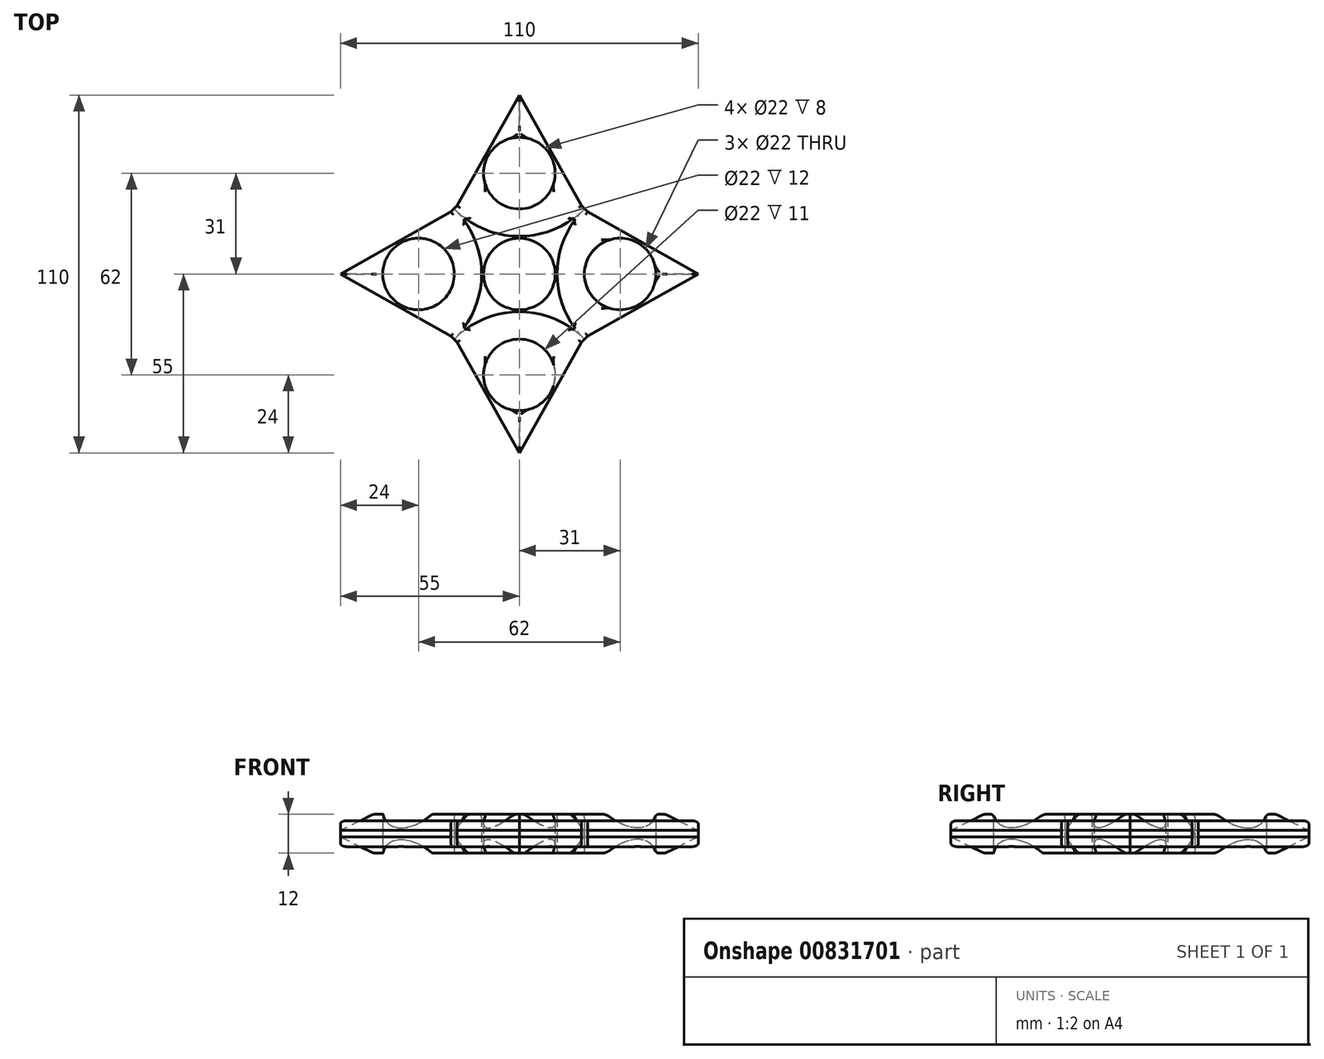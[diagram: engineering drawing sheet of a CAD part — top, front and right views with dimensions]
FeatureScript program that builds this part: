
annotation { "Feature Type Name" : "Feature", "Feature Type Description" : "" }
export const myFeature = defineFeature(function(context is Context, id is Id, definition is map)
    precondition{}
    {
        {
            var Q0;
            Q0=qCreatedBy(makeId("Top.planeOp"),FACE);
            var sketch = newSketch(context, id + "F0", { "sketchPlane" : qUnion([Q0])});
            skLineSegment(sketch, "E0.bottom", {"start": v(-55, 55) * mm, "end": v(55, 55) * mm});
            skLineSegment(sketch, "E0.top", {"start": v(-55, -55) * mm, "end": v(55, -55) * mm});
            skLineSegment(sketch, "E0.left", {"start": v(-55, 55) * mm, "end": v(-55, -55) * mm});
            skLineSegment(sketch, "E0.right", {"start": v(55, 55) * mm, "end": v(55, -55) * mm});
            skPoint(sketch, "E0.middle", {"position": v(0, 0) * mm});
            skCircle(sketch, "E1", {"center": v(0, 0) * mm, "radius": 11 * mm});
            skCircle(sketch, "E2", {"center": v(-31, 0) * mm, "radius": 11 * mm});
            skCircle(sketch, "E3.MirrorC", {"center": v(31, 0) * mm, "radius": 11 * mm});
            skCircle(sketch, "E4", {"center": v(0, 31) * mm, "radius": 11 * mm});
            skCircle(sketch, "E5.MirrorC", {"center": v(0, -31) * mm, "radius": 11 * mm});
            skLineSegment(sketch, "E6", {"start": v(0, 0) * mm, "end": v(-19.8, 19.8) * mm, "construction": true});
            skLineSegment(sketch, "E7.MirrorCS", {"start": v(0, 0) * mm, "end": v(19.8, 19.8) * mm, "construction": true});
            skLineSegment(sketch, "E8.MirrorCS", {"start": v(0, 0) * mm, "end": v(19.8, -19.8) * mm, "construction": true});
            skLineSegment(sketch, "E9.MirrorCS", {"start": v(0, 0) * mm, "end": v(-19.8, -19.8) * mm, "construction": true});
            skLineSegment(sketch, "E10", {"start": v(-55, 0) * mm, "end": v(-19.8, 19.8) * mm});
            skLineSegment(sketch, "E11", {"start": v(-19.8, 19.8) * mm, "end": v(0, 55) * mm});
            skLineSegment(sketch, "E12.MirrorCS", {"start": v(19.8, 19.8) * mm, "end": v(0, 55) * mm});
            skLineSegment(sketch, "E13.MirrorCS", {"start": v(55, 0) * mm, "end": v(19.8, 19.8) * mm});
            skLineSegment(sketch, "E14.MirrorCS", {"start": v(55, 0) * mm, "end": v(19.8, -19.8) * mm});
            skLineSegment(sketch, "E15.MirrorCS", {"start": v(19.8, -19.8) * mm, "end": v(0, -55) * mm});
            skLineSegment(sketch, "E16.MirrorCS", {"start": v(-19.8, -19.8) * mm, "end": v(0, -55) * mm});
            skLineSegment(sketch, "E17.MirrorCS", {"start": v(-55, 0) * mm, "end": v(-19.8, -19.8) * mm});
            skSolve(sketch);
        }
        {
            var Q0;
            Q0=makeQuery(id+"F0.imprint","IMPRINT",FACE,{"disambiguationData":[TD([[makeQuery(id+"F0.imprint","IMPRINT",EDGE,{"derivedFrom":sQuery(id+"F0.wireOp",EDGE,"E1")}),-1.0]])]});
            extrude(context, id + "F1", {"entities" : qUnion([Q0]), "depth" : 8 * mm, "offsetDistance" : 25 * mm});
        }
        {
            var Q0;
            Q0=makeQuery(id+"F1.opExtrude","CAP_FACE",FACE,{"disambiguationData":[OSD([sQuery(id+"F0.wireOp",EDGE,"E1"),sQuery(id+"F0.wireOp",EDGE,"E3.MirrorC"),sQuery(id+"F0.wireOp",EDGE,"E2"),sQuery(id+"F0.wireOp",EDGE,"E4"),sQuery(id+"F0.wireOp",EDGE,"E5.MirrorC"),sQuery(id+"F0.wireOp",EDGE,"E10"),sQuery(id+"F0.wireOp",EDGE,"E11"),sQuery(id+"F0.wireOp",EDGE,"E12.MirrorCS"),sQuery(id+"F0.wireOp",EDGE,"E13.MirrorCS"),sQuery(id+"F0.wireOp",EDGE,"E14.MirrorCS"),sQuery(id+"F0.wireOp",EDGE,"E15.MirrorCS"),sQuery(id+"F0.wireOp",EDGE,"E16.MirrorCS"),sQuery(id+"F0.wireOp",EDGE,"E17.MirrorCS")])],"isStart":false});
            var sketch = newSketch(context, id + "F2", { "sketchPlane" : qUnion([Q0])});
            skLineSegment(sketch, "E18", {"start": v(0, 0) * mm, "end": v(-19.8, 19.8) * mm, "construction": true});
            skLineSegment(sketch, "E19.MirrorCS", {"start": v(0, 0) * mm, "end": v(19.8, 19.8) * mm, "construction": true});
            skLineSegment(sketch, "E20.MirrorCS", {"start": v(0, 0) * mm, "end": v(-19.8, -19.8) * mm, "construction": true});
            skLineSegment(sketch, "E21.MirrorCS", {"start": v(0, 0) * mm, "end": v(19.8, -19.8) * mm, "construction": true});
            skArc(sketch, "E22", {"start": v(-19.8, -19.8) * mm, "mid": v(-11.6, 0) * mm, "end": v(-19.8, 19.8) * mm});
            skArc(sketch, "E23", {"start": v(-19.8, 19.8) * mm, "mid": v(0, 11.6) * mm, "end": v(19.8, 19.8) * mm});
            skArc(sketch, "E24", {"start": v(19.8, 19.8) * mm, "mid": v(11.6, 0) * mm, "end": v(19.8, -19.8) * mm});
            skArc(sketch, "E25", {"start": v(19.8, -19.8) * mm, "mid": v(0, -11.6) * mm, "end": v(-19.8, -19.8) * mm});
            skSolve(sketch);
        }
        {
            var Q0;
            Q0=makeQuery(id+"F2.imprint","IMPRINT",FACE,{"disambiguationData":[TD([[makeQuery(id+"F2.imprint","IMPRINT",EDGE,{"derivedFrom":sQuery(id+"F2.wireOp",EDGE,"E25")}),1.0]])]});
            var Q1;
            Q1=makeQuery(id+"F2.imprint","IMPRINT",FACE,{"disambiguationData":[TD([[makeQuery(id+"F2.imprint","IMPRINT",EDGE,{"derivedFrom":sQuery(id+"F2.wireOp",EDGE,"E22")}),1.0]])]});
            var Q2;
            Q2=makeQuery(id+"F2.imprint","IMPRINT",FACE,{"disambiguationData":[TD([[makeQuery(id+"F2.imprint","IMPRINT",EDGE,{"derivedFrom":sQuery(id+"F2.wireOp",EDGE,"E23")}),1.0]])]});
            var Q3;
            Q3=makeQuery(id+"F2.imprint","IMPRINT",FACE,{"disambiguationData":[TD([[makeQuery(id+"F2.imprint","IMPRINT",EDGE,{"derivedFrom":sQuery(id+"F2.wireOp",EDGE,"E24")}),1.0]])]});
            extrude(context, id + "F3", {"entities" : qUnion([Q0, Q1, Q2, Q3]), "depth" : 2 * mm, "offsetDistance" : 25 * mm, "hasSecondDirection" : true, "secondDirectionOppositeDirection" : true, "secondDirectionDepth" : 10 * mm});
        }
        {
            var Q0;
            Q0=makeQuery(id+"F3.opExtrude","CAP_EDGE",EDGE,{"disambiguationData":[OSD([sQuery(id+"F0.wireOp",EDGE,"E15.MirrorCS")])],"isStart":true});
            var Q1;
            Q1=makeQuery(id+"F3.opExtrude","CAP_EDGE",EDGE,{"disambiguationData":[OSD([sQuery(id+"F0.wireOp",EDGE,"E16.MirrorCS")])],"isStart":true});
            var Q2;
            Q2=makeQuery(id+"F3.opExtrude","CAP_EDGE",EDGE,{"disambiguationData":[OSD([sQuery(id+"F0.wireOp",EDGE,"E14.MirrorCS")])],"isStart":true});
            var Q3;
            Q3=makeQuery(id+"F3.opExtrude","CAP_EDGE",EDGE,{"disambiguationData":[OSD([sQuery(id+"F0.wireOp",EDGE,"E13.MirrorCS")])],"isStart":true});
            var Q4;
            Q4=makeQuery(id+"F3.opExtrude","CAP_EDGE",EDGE,{"disambiguationData":[OSD([sQuery(id+"F0.wireOp",EDGE,"E12.MirrorCS")])],"isStart":true});
            var Q5;
            Q5=makeQuery(id+"F3.opExtrude","CAP_EDGE",EDGE,{"disambiguationData":[OSD([sQuery(id+"F0.wireOp",EDGE,"E11")])],"isStart":true});
            var Q6;
            Q6=makeQuery(id+"F3.opExtrude","CAP_EDGE",EDGE,{"disambiguationData":[OSD([sQuery(id+"F0.wireOp",EDGE,"E10")])],"isStart":true});
            var Q7;
            Q7=makeQuery(id+"F3.opExtrude","CAP_EDGE",EDGE,{"disambiguationData":[OSD([sQuery(id+"F0.wireOp",EDGE,"E17.MirrorCS")])],"isStart":true});
            var Q8;
            Q8=makeQuery(id+"F3.opExtrude","CAP_EDGE",EDGE,{"disambiguationData":[OSD([sQuery(id+"F0.wireOp",EDGE,"E17.MirrorCS")])],"isStart":false});
            var Q9;
            Q9=makeQuery(id+"F3.opExtrude","CAP_EDGE",EDGE,{"disambiguationData":[OSD([sQuery(id+"F0.wireOp",EDGE,"E10")])],"isStart":false});
            var Q10;
            Q10=makeQuery(id+"F3.opExtrude","CAP_EDGE",EDGE,{"disambiguationData":[OSD([sQuery(id+"F0.wireOp",EDGE,"E11")])],"isStart":false});
            var Q11;
            Q11=makeQuery(id+"F3.opExtrude","CAP_EDGE",EDGE,{"disambiguationData":[OSD([sQuery(id+"F0.wireOp",EDGE,"E12.MirrorCS")])],"isStart":false});
            var Q12;
            Q12=makeQuery(id+"F3.opExtrude","CAP_EDGE",EDGE,{"disambiguationData":[OSD([sQuery(id+"F0.wireOp",EDGE,"E13.MirrorCS")])],"isStart":false});
            var Q13;
            Q13=makeQuery(id+"F3.opExtrude","CAP_EDGE",EDGE,{"disambiguationData":[OSD([sQuery(id+"F0.wireOp",EDGE,"E14.MirrorCS")])],"isStart":false});
            var Q14;
            Q14=makeQuery(id+"F3.opExtrude","CAP_EDGE",EDGE,{"disambiguationData":[OSD([sQuery(id+"F0.wireOp",EDGE,"E15.MirrorCS")])],"isStart":false});
            var Q15;
            Q15=makeQuery(id+"F3.opExtrude","CAP_EDGE",EDGE,{"disambiguationData":[OSD([sQuery(id+"F0.wireOp",EDGE,"E16.MirrorCS")])],"isStart":false});
            chamfer(context, id + "F4", {"entities" : qUnion([Q0, Q1, Q2, Q3, Q4, Q5, Q6, Q7, Q8, Q9, Q10, Q11, Q12, Q13, Q14, Q15]), "width" : 5 * mm, "tangentPropagation" : true});
        }
        {
            var Q0;
            Q0=makeQuery(id+"F1.opExtrude","SWEPT_EDGE",EDGE,{"disambiguationData":[OSD([sQuery(id+"F0.wireOp",EDGE,"E16.MirrorCS"),sQuery(id+"F0.wireOp",EDGE,"E17.MirrorCS")])]});
            var Q1;
            Q1=makeQuery(id+"F1.opExtrude","SWEPT_EDGE",EDGE,{"disambiguationData":[OSD([sQuery(id+"F0.wireOp",EDGE,"E10"),sQuery(id+"F0.wireOp",EDGE,"E11")])]});
            var Q2;
            Q2=makeQuery(id+"F1.opExtrude","SWEPT_EDGE",EDGE,{"disambiguationData":[OSD([sQuery(id+"F0.wireOp",EDGE,"E12.MirrorCS"),sQuery(id+"F0.wireOp",EDGE,"E13.MirrorCS")])]});
            var Q3;
            Q3=makeQuery(id+"F1.opExtrude","SWEPT_EDGE",EDGE,{"disambiguationData":[OSD([sQuery(id+"F0.wireOp",EDGE,"E14.MirrorCS"),sQuery(id+"F0.wireOp",EDGE,"E15.MirrorCS")])]});
            chamfer(context, id + "F5", {"entities" : qUnion([Q0, Q1, Q2, Q3]), "width" : 5 * mm, "tangentPropagation" : true});
        }
        {
            var Q0;
            Q0=makeQuery(id+"F1.opExtrude","CAP_EDGE",EDGE,{"disambiguationData":[OSD([sQuery(id+"F0.wireOp",EDGE,"E12.MirrorCS")])],"isStart":false});
            var Q1;
            {var subQ0=sQuery(id+"F0.wireOp",EDGE,"E13.MirrorCS");var subQ1=sQuery(id+"F0.wireOp",EDGE,"E12.MirrorCS");Q1=makeQuery(id+"F5.opChamfer","BLEND_EDGE",EDGE,{"blendedFrom":[makeQuery(id+"F1.opExtrude","SWEPT_EDGE",EDGE,{"disambiguationData":[OSD([subQ1,subQ0])]}),makeQuery(id+"F1.opExtrude","CAP_FACE",FACE,{"disambiguationData":[OSD([sQuery(id+"F0.wireOp",EDGE,"E1"),sQuery(id+"F0.wireOp",EDGE,"E3.MirrorC"),sQuery(id+"F0.wireOp",EDGE,"E2"),sQuery(id+"F0.wireOp",EDGE,"E4"),sQuery(id+"F0.wireOp",EDGE,"E5.MirrorC"),sQuery(id+"F0.wireOp",EDGE,"E10"),sQuery(id+"F0.wireOp",EDGE,"E11"),subQ1,subQ0,sQuery(id+"F0.wireOp",EDGE,"E14.MirrorCS"),sQuery(id+"F0.wireOp",EDGE,"E15.MirrorCS"),sQuery(id+"F0.wireOp",EDGE,"E16.MirrorCS"),sQuery(id+"F0.wireOp",EDGE,"E17.MirrorCS")])],"isStart":false})],"blendedInto":[makeQuery(id+"F1.opExtrude","CAP_FACE",FACE,{"disambiguationData":[OSD([sQuery(id+"F0.wireOp",EDGE,"E1"),sQuery(id+"F0.wireOp",EDGE,"E3.MirrorC"),sQuery(id+"F0.wireOp",EDGE,"E2"),sQuery(id+"F0.wireOp",EDGE,"E4"),sQuery(id+"F0.wireOp",EDGE,"E5.MirrorC"),sQuery(id+"F0.wireOp",EDGE,"E10"),sQuery(id+"F0.wireOp",EDGE,"E11"),subQ1,subQ0,sQuery(id+"F0.wireOp",EDGE,"E14.MirrorCS"),sQuery(id+"F0.wireOp",EDGE,"E15.MirrorCS"),sQuery(id+"F0.wireOp",EDGE,"E16.MirrorCS"),sQuery(id+"F0.wireOp",EDGE,"E17.MirrorCS")])],"isStart":false})]});}
            var Q2;
            Q2=makeQuery(id+"F1.opExtrude","CAP_EDGE",EDGE,{"disambiguationData":[OSD([sQuery(id+"F0.wireOp",EDGE,"E13.MirrorCS")])],"isStart":false});
            var Q3;
            Q3=makeQuery(id+"F1.opExtrude","CAP_EDGE",EDGE,{"disambiguationData":[OSD([sQuery(id+"F0.wireOp",EDGE,"E14.MirrorCS")])],"isStart":false});
            var Q4;
            {var subQ0=sQuery(id+"F0.wireOp",EDGE,"E15.MirrorCS");var subQ1=sQuery(id+"F0.wireOp",EDGE,"E14.MirrorCS");Q4=makeQuery(id+"F5.opChamfer","BLEND_EDGE",EDGE,{"blendedFrom":[makeQuery(id+"F1.opExtrude","SWEPT_EDGE",EDGE,{"disambiguationData":[OSD([subQ1,subQ0])]}),makeQuery(id+"F1.opExtrude","CAP_FACE",FACE,{"disambiguationData":[OSD([sQuery(id+"F0.wireOp",EDGE,"E1"),sQuery(id+"F0.wireOp",EDGE,"E3.MirrorC"),sQuery(id+"F0.wireOp",EDGE,"E2"),sQuery(id+"F0.wireOp",EDGE,"E4"),sQuery(id+"F0.wireOp",EDGE,"E5.MirrorC"),sQuery(id+"F0.wireOp",EDGE,"E10"),sQuery(id+"F0.wireOp",EDGE,"E11"),sQuery(id+"F0.wireOp",EDGE,"E12.MirrorCS"),sQuery(id+"F0.wireOp",EDGE,"E13.MirrorCS"),subQ1,subQ0,sQuery(id+"F0.wireOp",EDGE,"E16.MirrorCS"),sQuery(id+"F0.wireOp",EDGE,"E17.MirrorCS")])],"isStart":false})],"blendedInto":[makeQuery(id+"F1.opExtrude","CAP_FACE",FACE,{"disambiguationData":[OSD([sQuery(id+"F0.wireOp",EDGE,"E1"),sQuery(id+"F0.wireOp",EDGE,"E3.MirrorC"),sQuery(id+"F0.wireOp",EDGE,"E2"),sQuery(id+"F0.wireOp",EDGE,"E4"),sQuery(id+"F0.wireOp",EDGE,"E5.MirrorC"),sQuery(id+"F0.wireOp",EDGE,"E10"),sQuery(id+"F0.wireOp",EDGE,"E11"),sQuery(id+"F0.wireOp",EDGE,"E12.MirrorCS"),sQuery(id+"F0.wireOp",EDGE,"E13.MirrorCS"),subQ1,subQ0,sQuery(id+"F0.wireOp",EDGE,"E16.MirrorCS"),sQuery(id+"F0.wireOp",EDGE,"E17.MirrorCS")])],"isStart":false})]});}
            var Q5;
            Q5=makeQuery(id+"F1.opExtrude","CAP_EDGE",EDGE,{"disambiguationData":[OSD([sQuery(id+"F0.wireOp",EDGE,"E15.MirrorCS")])],"isStart":false});
            var Q6;
            Q6=makeQuery(id+"F1.opExtrude","CAP_EDGE",EDGE,{"disambiguationData":[OSD([sQuery(id+"F0.wireOp",EDGE,"E16.MirrorCS")])],"isStart":false});
            var Q7;
            {var subQ0=sQuery(id+"F0.wireOp",EDGE,"E17.MirrorCS");var subQ1=sQuery(id+"F0.wireOp",EDGE,"E16.MirrorCS");Q7=makeQuery(id+"F5.opChamfer","BLEND_EDGE",EDGE,{"blendedFrom":[makeQuery(id+"F1.opExtrude","SWEPT_EDGE",EDGE,{"disambiguationData":[OSD([subQ1,subQ0])]}),makeQuery(id+"F1.opExtrude","CAP_FACE",FACE,{"disambiguationData":[OSD([sQuery(id+"F0.wireOp",EDGE,"E1"),sQuery(id+"F0.wireOp",EDGE,"E3.MirrorC"),sQuery(id+"F0.wireOp",EDGE,"E2"),sQuery(id+"F0.wireOp",EDGE,"E4"),sQuery(id+"F0.wireOp",EDGE,"E5.MirrorC"),sQuery(id+"F0.wireOp",EDGE,"E10"),sQuery(id+"F0.wireOp",EDGE,"E11"),sQuery(id+"F0.wireOp",EDGE,"E12.MirrorCS"),sQuery(id+"F0.wireOp",EDGE,"E13.MirrorCS"),sQuery(id+"F0.wireOp",EDGE,"E14.MirrorCS"),sQuery(id+"F0.wireOp",EDGE,"E15.MirrorCS"),subQ1,subQ0])],"isStart":false})],"blendedInto":[makeQuery(id+"F1.opExtrude","CAP_FACE",FACE,{"disambiguationData":[OSD([sQuery(id+"F0.wireOp",EDGE,"E1"),sQuery(id+"F0.wireOp",EDGE,"E3.MirrorC"),sQuery(id+"F0.wireOp",EDGE,"E2"),sQuery(id+"F0.wireOp",EDGE,"E4"),sQuery(id+"F0.wireOp",EDGE,"E5.MirrorC"),sQuery(id+"F0.wireOp",EDGE,"E10"),sQuery(id+"F0.wireOp",EDGE,"E11"),sQuery(id+"F0.wireOp",EDGE,"E12.MirrorCS"),sQuery(id+"F0.wireOp",EDGE,"E13.MirrorCS"),sQuery(id+"F0.wireOp",EDGE,"E14.MirrorCS"),sQuery(id+"F0.wireOp",EDGE,"E15.MirrorCS"),subQ1,subQ0])],"isStart":false})]});}
            var Q8;
            Q8=makeQuery(id+"F1.opExtrude","CAP_EDGE",EDGE,{"disambiguationData":[OSD([sQuery(id+"F0.wireOp",EDGE,"E17.MirrorCS")])],"isStart":false});
            var Q9;
            Q9=makeQuery(id+"F1.opExtrude","CAP_EDGE",EDGE,{"disambiguationData":[OSD([sQuery(id+"F0.wireOp",EDGE,"E10")])],"isStart":false});
            var Q10;
            {var subQ0=sQuery(id+"F0.wireOp",EDGE,"E11");var subQ1=sQuery(id+"F0.wireOp",EDGE,"E10");Q10=makeQuery(id+"F5.opChamfer","BLEND_EDGE",EDGE,{"blendedFrom":[makeQuery(id+"F1.opExtrude","SWEPT_EDGE",EDGE,{"disambiguationData":[OSD([subQ1,subQ0])]}),makeQuery(id+"F1.opExtrude","CAP_FACE",FACE,{"disambiguationData":[OSD([sQuery(id+"F0.wireOp",EDGE,"E1"),sQuery(id+"F0.wireOp",EDGE,"E3.MirrorC"),sQuery(id+"F0.wireOp",EDGE,"E2"),sQuery(id+"F0.wireOp",EDGE,"E4"),sQuery(id+"F0.wireOp",EDGE,"E5.MirrorC"),subQ1,subQ0,sQuery(id+"F0.wireOp",EDGE,"E12.MirrorCS"),sQuery(id+"F0.wireOp",EDGE,"E13.MirrorCS"),sQuery(id+"F0.wireOp",EDGE,"E14.MirrorCS"),sQuery(id+"F0.wireOp",EDGE,"E15.MirrorCS"),sQuery(id+"F0.wireOp",EDGE,"E16.MirrorCS"),sQuery(id+"F0.wireOp",EDGE,"E17.MirrorCS")])],"isStart":false})],"blendedInto":[makeQuery(id+"F1.opExtrude","CAP_FACE",FACE,{"disambiguationData":[OSD([sQuery(id+"F0.wireOp",EDGE,"E1"),sQuery(id+"F0.wireOp",EDGE,"E3.MirrorC"),sQuery(id+"F0.wireOp",EDGE,"E2"),sQuery(id+"F0.wireOp",EDGE,"E4"),sQuery(id+"F0.wireOp",EDGE,"E5.MirrorC"),subQ1,subQ0,sQuery(id+"F0.wireOp",EDGE,"E12.MirrorCS"),sQuery(id+"F0.wireOp",EDGE,"E13.MirrorCS"),sQuery(id+"F0.wireOp",EDGE,"E14.MirrorCS"),sQuery(id+"F0.wireOp",EDGE,"E15.MirrorCS"),sQuery(id+"F0.wireOp",EDGE,"E16.MirrorCS"),sQuery(id+"F0.wireOp",EDGE,"E17.MirrorCS")])],"isStart":false})]});}
            var Q11;
            Q11=makeQuery(id+"F1.opExtrude","CAP_EDGE",EDGE,{"disambiguationData":[OSD([sQuery(id+"F0.wireOp",EDGE,"E11")])],"isStart":false});
            var Q12;
            {var subQ0=sQuery(id+"F0.wireOp",EDGE,"E17.MirrorCS");var subQ1=sQuery(id+"F0.wireOp",EDGE,"E16.MirrorCS");Q12=makeQuery(id+"F5.opChamfer","BLEND_EDGE",EDGE,{"blendedFrom":[makeQuery(id+"F1.opExtrude","SWEPT_EDGE",EDGE,{"disambiguationData":[OSD([subQ1,subQ0])]}),makeQuery(id+"F1.opExtrude","CAP_FACE",FACE,{"disambiguationData":[OSD([sQuery(id+"F0.wireOp",EDGE,"E1"),sQuery(id+"F0.wireOp",EDGE,"E3.MirrorC"),sQuery(id+"F0.wireOp",EDGE,"E2"),sQuery(id+"F0.wireOp",EDGE,"E4"),sQuery(id+"F0.wireOp",EDGE,"E5.MirrorC"),sQuery(id+"F0.wireOp",EDGE,"E10"),sQuery(id+"F0.wireOp",EDGE,"E11"),sQuery(id+"F0.wireOp",EDGE,"E12.MirrorCS"),sQuery(id+"F0.wireOp",EDGE,"E13.MirrorCS"),sQuery(id+"F0.wireOp",EDGE,"E14.MirrorCS"),sQuery(id+"F0.wireOp",EDGE,"E15.MirrorCS"),subQ1,subQ0])],"isStart":true})],"blendedInto":[makeQuery(id+"F1.opExtrude","CAP_FACE",FACE,{"disambiguationData":[OSD([sQuery(id+"F0.wireOp",EDGE,"E1"),sQuery(id+"F0.wireOp",EDGE,"E3.MirrorC"),sQuery(id+"F0.wireOp",EDGE,"E2"),sQuery(id+"F0.wireOp",EDGE,"E4"),sQuery(id+"F0.wireOp",EDGE,"E5.MirrorC"),sQuery(id+"F0.wireOp",EDGE,"E10"),sQuery(id+"F0.wireOp",EDGE,"E11"),sQuery(id+"F0.wireOp",EDGE,"E12.MirrorCS"),sQuery(id+"F0.wireOp",EDGE,"E13.MirrorCS"),sQuery(id+"F0.wireOp",EDGE,"E14.MirrorCS"),sQuery(id+"F0.wireOp",EDGE,"E15.MirrorCS"),subQ1,subQ0])],"isStart":true})]});}
            var Q13;
            Q13=makeQuery(id+"F1.opExtrude","CAP_EDGE",EDGE,{"disambiguationData":[OSD([sQuery(id+"F0.wireOp",EDGE,"E17.MirrorCS")])],"isStart":true});
            var Q14;
            Q14=makeQuery(id+"F1.opExtrude","CAP_EDGE",EDGE,{"disambiguationData":[OSD([sQuery(id+"F0.wireOp",EDGE,"E16.MirrorCS")])],"isStart":true});
            var Q15;
            Q15=makeQuery(id+"F1.opExtrude","CAP_EDGE",EDGE,{"disambiguationData":[OSD([sQuery(id+"F0.wireOp",EDGE,"E15.MirrorCS")])],"isStart":true});
            var Q16;
            {var subQ0=sQuery(id+"F0.wireOp",EDGE,"E15.MirrorCS");var subQ1=sQuery(id+"F0.wireOp",EDGE,"E14.MirrorCS");Q16=makeQuery(id+"F5.opChamfer","BLEND_EDGE",EDGE,{"blendedFrom":[makeQuery(id+"F1.opExtrude","SWEPT_EDGE",EDGE,{"disambiguationData":[OSD([subQ1,subQ0])]}),makeQuery(id+"F1.opExtrude","CAP_FACE",FACE,{"disambiguationData":[OSD([sQuery(id+"F0.wireOp",EDGE,"E1"),sQuery(id+"F0.wireOp",EDGE,"E3.MirrorC"),sQuery(id+"F0.wireOp",EDGE,"E2"),sQuery(id+"F0.wireOp",EDGE,"E4"),sQuery(id+"F0.wireOp",EDGE,"E5.MirrorC"),sQuery(id+"F0.wireOp",EDGE,"E10"),sQuery(id+"F0.wireOp",EDGE,"E11"),sQuery(id+"F0.wireOp",EDGE,"E12.MirrorCS"),sQuery(id+"F0.wireOp",EDGE,"E13.MirrorCS"),subQ1,subQ0,sQuery(id+"F0.wireOp",EDGE,"E16.MirrorCS"),sQuery(id+"F0.wireOp",EDGE,"E17.MirrorCS")])],"isStart":true})],"blendedInto":[makeQuery(id+"F1.opExtrude","CAP_FACE",FACE,{"disambiguationData":[OSD([sQuery(id+"F0.wireOp",EDGE,"E1"),sQuery(id+"F0.wireOp",EDGE,"E3.MirrorC"),sQuery(id+"F0.wireOp",EDGE,"E2"),sQuery(id+"F0.wireOp",EDGE,"E4"),sQuery(id+"F0.wireOp",EDGE,"E5.MirrorC"),sQuery(id+"F0.wireOp",EDGE,"E10"),sQuery(id+"F0.wireOp",EDGE,"E11"),sQuery(id+"F0.wireOp",EDGE,"E12.MirrorCS"),sQuery(id+"F0.wireOp",EDGE,"E13.MirrorCS"),subQ1,subQ0,sQuery(id+"F0.wireOp",EDGE,"E16.MirrorCS"),sQuery(id+"F0.wireOp",EDGE,"E17.MirrorCS")])],"isStart":true})]});}
            var Q17;
            Q17=makeQuery(id+"F1.opExtrude","CAP_EDGE",EDGE,{"disambiguationData":[OSD([sQuery(id+"F0.wireOp",EDGE,"E14.MirrorCS")])],"isStart":true});
            var Q18;
            Q18=makeQuery(id+"F1.opExtrude","CAP_EDGE",EDGE,{"disambiguationData":[OSD([sQuery(id+"F0.wireOp",EDGE,"E10")])],"isStart":true});
            var Q19;
            {var subQ0=sQuery(id+"F0.wireOp",EDGE,"E11");var subQ1=sQuery(id+"F0.wireOp",EDGE,"E10");Q19=makeQuery(id+"F5.opChamfer","BLEND_EDGE",EDGE,{"blendedFrom":[makeQuery(id+"F1.opExtrude","SWEPT_EDGE",EDGE,{"disambiguationData":[OSD([subQ1,subQ0])]}),makeQuery(id+"F1.opExtrude","CAP_FACE",FACE,{"disambiguationData":[OSD([sQuery(id+"F0.wireOp",EDGE,"E1"),sQuery(id+"F0.wireOp",EDGE,"E3.MirrorC"),sQuery(id+"F0.wireOp",EDGE,"E2"),sQuery(id+"F0.wireOp",EDGE,"E4"),sQuery(id+"F0.wireOp",EDGE,"E5.MirrorC"),subQ1,subQ0,sQuery(id+"F0.wireOp",EDGE,"E12.MirrorCS"),sQuery(id+"F0.wireOp",EDGE,"E13.MirrorCS"),sQuery(id+"F0.wireOp",EDGE,"E14.MirrorCS"),sQuery(id+"F0.wireOp",EDGE,"E15.MirrorCS"),sQuery(id+"F0.wireOp",EDGE,"E16.MirrorCS"),sQuery(id+"F0.wireOp",EDGE,"E17.MirrorCS")])],"isStart":true})],"blendedInto":[makeQuery(id+"F1.opExtrude","CAP_FACE",FACE,{"disambiguationData":[OSD([sQuery(id+"F0.wireOp",EDGE,"E1"),sQuery(id+"F0.wireOp",EDGE,"E3.MirrorC"),sQuery(id+"F0.wireOp",EDGE,"E2"),sQuery(id+"F0.wireOp",EDGE,"E4"),sQuery(id+"F0.wireOp",EDGE,"E5.MirrorC"),subQ1,subQ0,sQuery(id+"F0.wireOp",EDGE,"E12.MirrorCS"),sQuery(id+"F0.wireOp",EDGE,"E13.MirrorCS"),sQuery(id+"F0.wireOp",EDGE,"E14.MirrorCS"),sQuery(id+"F0.wireOp",EDGE,"E15.MirrorCS"),sQuery(id+"F0.wireOp",EDGE,"E16.MirrorCS"),sQuery(id+"F0.wireOp",EDGE,"E17.MirrorCS")])],"isStart":true})]});}
            var Q20;
            Q20=makeQuery(id+"F1.opExtrude","CAP_EDGE",EDGE,{"disambiguationData":[OSD([sQuery(id+"F0.wireOp",EDGE,"E11")])],"isStart":true});
            var Q21;
            Q21=makeQuery(id+"F1.opExtrude","CAP_EDGE",EDGE,{"disambiguationData":[OSD([sQuery(id+"F0.wireOp",EDGE,"E12.MirrorCS")])],"isStart":true});
            var Q22;
            {var subQ0=sQuery(id+"F0.wireOp",EDGE,"E13.MirrorCS");var subQ1=sQuery(id+"F0.wireOp",EDGE,"E12.MirrorCS");Q22=makeQuery(id+"F5.opChamfer","BLEND_EDGE",EDGE,{"blendedFrom":[makeQuery(id+"F1.opExtrude","SWEPT_EDGE",EDGE,{"disambiguationData":[OSD([subQ1,subQ0])]}),makeQuery(id+"F1.opExtrude","CAP_FACE",FACE,{"disambiguationData":[OSD([sQuery(id+"F0.wireOp",EDGE,"E1"),sQuery(id+"F0.wireOp",EDGE,"E3.MirrorC"),sQuery(id+"F0.wireOp",EDGE,"E2"),sQuery(id+"F0.wireOp",EDGE,"E4"),sQuery(id+"F0.wireOp",EDGE,"E5.MirrorC"),sQuery(id+"F0.wireOp",EDGE,"E10"),sQuery(id+"F0.wireOp",EDGE,"E11"),subQ1,subQ0,sQuery(id+"F0.wireOp",EDGE,"E14.MirrorCS"),sQuery(id+"F0.wireOp",EDGE,"E15.MirrorCS"),sQuery(id+"F0.wireOp",EDGE,"E16.MirrorCS"),sQuery(id+"F0.wireOp",EDGE,"E17.MirrorCS")])],"isStart":true})],"blendedInto":[makeQuery(id+"F1.opExtrude","CAP_FACE",FACE,{"disambiguationData":[OSD([sQuery(id+"F0.wireOp",EDGE,"E1"),sQuery(id+"F0.wireOp",EDGE,"E3.MirrorC"),sQuery(id+"F0.wireOp",EDGE,"E2"),sQuery(id+"F0.wireOp",EDGE,"E4"),sQuery(id+"F0.wireOp",EDGE,"E5.MirrorC"),sQuery(id+"F0.wireOp",EDGE,"E10"),sQuery(id+"F0.wireOp",EDGE,"E11"),subQ1,subQ0,sQuery(id+"F0.wireOp",EDGE,"E14.MirrorCS"),sQuery(id+"F0.wireOp",EDGE,"E15.MirrorCS"),sQuery(id+"F0.wireOp",EDGE,"E16.MirrorCS"),sQuery(id+"F0.wireOp",EDGE,"E17.MirrorCS")])],"isStart":true})]});}
            var Q23;
            Q23=makeQuery(id+"F1.opExtrude","CAP_EDGE",EDGE,{"disambiguationData":[OSD([sQuery(id+"F0.wireOp",EDGE,"E13.MirrorCS")])],"isStart":true});
            var Q24;
            {var subQ0=sQuery(id+"F0.wireOp",EDGE,"E12.MirrorCS");Q24=makeQuery(id+"F4.opChamfer","BLEND_EDGE",EDGE,{"blendedFrom":[makeQuery(id+"F3.opExtrude","CAP_EDGE",EDGE,{"disambiguationData":[OSD([subQ0])],"isStart":true}),makeQuery(id+"F3.opExtrude","CAP_FACE",FACE,{"disambiguationData":[OSD([sQuery(id+"F0.wireOp",EDGE,"E4"),sQuery(id+"F0.wireOp",EDGE,"E11"),subQ0,sQuery(id+"F2.wireOp",EDGE,"E23")])],"isStart":true})],"blendedInto":[makeQuery(id+"F3.opExtrude","CAP_FACE",FACE,{"disambiguationData":[OSD([sQuery(id+"F0.wireOp",EDGE,"E4"),sQuery(id+"F0.wireOp",EDGE,"E11"),subQ0,sQuery(id+"F2.wireOp",EDGE,"E23")])],"isStart":true})]});}
            var Q25;
            {var subQ0=sQuery(id+"F0.wireOp",EDGE,"E13.MirrorCS");Q25=makeQuery(id+"F4.opChamfer","BLEND_EDGE",EDGE,{"blendedFrom":[makeQuery(id+"F3.opExtrude","CAP_EDGE",EDGE,{"disambiguationData":[OSD([subQ0])],"isStart":true}),makeQuery(id+"F3.opExtrude","CAP_FACE",FACE,{"disambiguationData":[OSD([sQuery(id+"F0.wireOp",EDGE,"E3.MirrorC"),subQ0,sQuery(id+"F0.wireOp",EDGE,"E14.MirrorCS"),sQuery(id+"F2.wireOp",EDGE,"E24")])],"isStart":true})],"blendedInto":[makeQuery(id+"F3.opExtrude","CAP_FACE",FACE,{"disambiguationData":[OSD([sQuery(id+"F0.wireOp",EDGE,"E3.MirrorC"),subQ0,sQuery(id+"F0.wireOp",EDGE,"E14.MirrorCS"),sQuery(id+"F2.wireOp",EDGE,"E24")])],"isStart":true})]});}
            var Q26;
            {var subQ0=sQuery(id+"F0.wireOp",EDGE,"E11");Q26=makeQuery(id+"F4.opChamfer","BLEND_EDGE",EDGE,{"blendedFrom":[makeQuery(id+"F3.opExtrude","CAP_EDGE",EDGE,{"disambiguationData":[OSD([subQ0])],"isStart":true}),makeQuery(id+"F3.opExtrude","CAP_FACE",FACE,{"disambiguationData":[OSD([sQuery(id+"F0.wireOp",EDGE,"E4"),subQ0,sQuery(id+"F0.wireOp",EDGE,"E12.MirrorCS"),sQuery(id+"F2.wireOp",EDGE,"E23")])],"isStart":true})],"blendedInto":[makeQuery(id+"F3.opExtrude","CAP_FACE",FACE,{"disambiguationData":[OSD([sQuery(id+"F0.wireOp",EDGE,"E4"),subQ0,sQuery(id+"F0.wireOp",EDGE,"E12.MirrorCS"),sQuery(id+"F2.wireOp",EDGE,"E23")])],"isStart":true})]});}
            var Q27;
            {var subQ0=sQuery(id+"F0.wireOp",EDGE,"E10");Q27=makeQuery(id+"F4.opChamfer","BLEND_EDGE",EDGE,{"blendedFrom":[makeQuery(id+"F3.opExtrude","CAP_EDGE",EDGE,{"disambiguationData":[OSD([subQ0])],"isStart":true}),makeQuery(id+"F3.opExtrude","CAP_FACE",FACE,{"disambiguationData":[OSD([sQuery(id+"F0.wireOp",EDGE,"E2"),subQ0,sQuery(id+"F0.wireOp",EDGE,"E17.MirrorCS"),sQuery(id+"F2.wireOp",EDGE,"E22")])],"isStart":true})],"blendedInto":[makeQuery(id+"F3.opExtrude","CAP_FACE",FACE,{"disambiguationData":[OSD([sQuery(id+"F0.wireOp",EDGE,"E2"),subQ0,sQuery(id+"F0.wireOp",EDGE,"E17.MirrorCS"),sQuery(id+"F2.wireOp",EDGE,"E22")])],"isStart":true})]});}
            var Q28;
            {var subQ0=sQuery(id+"F0.wireOp",EDGE,"E17.MirrorCS");Q28=makeQuery(id+"F4.opChamfer","BLEND_EDGE",EDGE,{"blendedFrom":[makeQuery(id+"F3.opExtrude","CAP_EDGE",EDGE,{"disambiguationData":[OSD([subQ0])],"isStart":true}),makeQuery(id+"F3.opExtrude","CAP_FACE",FACE,{"disambiguationData":[OSD([sQuery(id+"F0.wireOp",EDGE,"E2"),sQuery(id+"F0.wireOp",EDGE,"E10"),subQ0,sQuery(id+"F2.wireOp",EDGE,"E22")])],"isStart":true})],"blendedInto":[makeQuery(id+"F3.opExtrude","CAP_FACE",FACE,{"disambiguationData":[OSD([sQuery(id+"F0.wireOp",EDGE,"E2"),sQuery(id+"F0.wireOp",EDGE,"E10"),subQ0,sQuery(id+"F2.wireOp",EDGE,"E22")])],"isStart":true})]});}
            var Q29;
            {var subQ0=sQuery(id+"F0.wireOp",EDGE,"E16.MirrorCS");Q29=makeQuery(id+"F4.opChamfer","BLEND_EDGE",EDGE,{"blendedFrom":[makeQuery(id+"F3.opExtrude","CAP_EDGE",EDGE,{"disambiguationData":[OSD([subQ0])],"isStart":true}),makeQuery(id+"F3.opExtrude","CAP_FACE",FACE,{"disambiguationData":[OSD([sQuery(id+"F0.wireOp",EDGE,"E5.MirrorC"),sQuery(id+"F0.wireOp",EDGE,"E15.MirrorCS"),subQ0,sQuery(id+"F2.wireOp",EDGE,"E25")])],"isStart":true})],"blendedInto":[makeQuery(id+"F3.opExtrude","CAP_FACE",FACE,{"disambiguationData":[OSD([sQuery(id+"F0.wireOp",EDGE,"E5.MirrorC"),sQuery(id+"F0.wireOp",EDGE,"E15.MirrorCS"),subQ0,sQuery(id+"F2.wireOp",EDGE,"E25")])],"isStart":true})]});}
            var Q30;
            {var subQ0=sQuery(id+"F0.wireOp",EDGE,"E15.MirrorCS");Q30=makeQuery(id+"F4.opChamfer","BLEND_EDGE",EDGE,{"blendedFrom":[makeQuery(id+"F3.opExtrude","CAP_EDGE",EDGE,{"disambiguationData":[OSD([subQ0])],"isStart":true}),makeQuery(id+"F3.opExtrude","CAP_FACE",FACE,{"disambiguationData":[OSD([sQuery(id+"F0.wireOp",EDGE,"E5.MirrorC"),subQ0,sQuery(id+"F0.wireOp",EDGE,"E16.MirrorCS"),sQuery(id+"F2.wireOp",EDGE,"E25")])],"isStart":true})],"blendedInto":[makeQuery(id+"F3.opExtrude","CAP_FACE",FACE,{"disambiguationData":[OSD([sQuery(id+"F0.wireOp",EDGE,"E5.MirrorC"),subQ0,sQuery(id+"F0.wireOp",EDGE,"E16.MirrorCS"),sQuery(id+"F2.wireOp",EDGE,"E25")])],"isStart":true})]});}
            var Q31;
            {var subQ0=sQuery(id+"F0.wireOp",EDGE,"E14.MirrorCS");Q31=makeQuery(id+"F4.opChamfer","BLEND_EDGE",EDGE,{"blendedFrom":[makeQuery(id+"F3.opExtrude","CAP_EDGE",EDGE,{"disambiguationData":[OSD([subQ0])],"isStart":true}),makeQuery(id+"F3.opExtrude","CAP_FACE",FACE,{"disambiguationData":[OSD([sQuery(id+"F0.wireOp",EDGE,"E3.MirrorC"),sQuery(id+"F0.wireOp",EDGE,"E13.MirrorCS"),subQ0,sQuery(id+"F2.wireOp",EDGE,"E24")])],"isStart":true})],"blendedInto":[makeQuery(id+"F3.opExtrude","CAP_FACE",FACE,{"disambiguationData":[OSD([sQuery(id+"F0.wireOp",EDGE,"E3.MirrorC"),sQuery(id+"F0.wireOp",EDGE,"E13.MirrorCS"),subQ0,sQuery(id+"F2.wireOp",EDGE,"E24")])],"isStart":true})]});}
            var Q32;
            Q32=makeQuery(id+"F3.opExtrude","CAP_EDGE",EDGE,{"disambiguationData":[OSD([sQuery(id+"F2.wireOp",EDGE,"E25")])],"isStart":true});
            var Q33;
            Q33=makeQuery(id+"F3.opExtrude","CAP_EDGE",EDGE,{"disambiguationData":[OSD([sQuery(id+"F2.wireOp",EDGE,"E24")])],"isStart":true});
            var Q34;
            Q34=makeQuery(id+"F3.opExtrude","CAP_EDGE",EDGE,{"disambiguationData":[OSD([sQuery(id+"F2.wireOp",EDGE,"E22")])],"isStart":true});
            var Q35;
            Q35=makeQuery(id+"F3.opExtrude","CAP_EDGE",EDGE,{"disambiguationData":[OSD([sQuery(id+"F2.wireOp",EDGE,"E23")])],"isStart":true});
            var Q36;
            Q36=makeQuery(id+"F1.opExtrude","CAP_EDGE",EDGE,{"disambiguationData":[OSD([sQuery(id+"F0.wireOp",EDGE,"E1")])],"isStart":true});
            var Q37;
            {var subQ0=sQuery(id+"F0.wireOp",EDGE,"E10");Q37=makeQuery(id+"F4.opChamfer","BLEND_EDGE",EDGE,{"blendedFrom":[makeQuery(id+"F3.opExtrude","CAP_EDGE",EDGE,{"disambiguationData":[OSD([subQ0])],"isStart":false}),makeQuery(id+"F3.opExtrude","CAP_FACE",FACE,{"disambiguationData":[OSD([sQuery(id+"F0.wireOp",EDGE,"E2"),subQ0,sQuery(id+"F0.wireOp",EDGE,"E17.MirrorCS"),sQuery(id+"F2.wireOp",EDGE,"E22")])],"isStart":false})],"blendedInto":[makeQuery(id+"F3.opExtrude","CAP_FACE",FACE,{"disambiguationData":[OSD([sQuery(id+"F0.wireOp",EDGE,"E2"),subQ0,sQuery(id+"F0.wireOp",EDGE,"E17.MirrorCS"),sQuery(id+"F2.wireOp",EDGE,"E22")])],"isStart":false})]});}
            var Q38;
            {var subQ0=sQuery(id+"F0.wireOp",EDGE,"E17.MirrorCS");Q38=makeQuery(id+"F4.opChamfer","BLEND_EDGE",EDGE,{"blendedFrom":[makeQuery(id+"F3.opExtrude","CAP_EDGE",EDGE,{"disambiguationData":[OSD([subQ0])],"isStart":false}),makeQuery(id+"F3.opExtrude","CAP_FACE",FACE,{"disambiguationData":[OSD([sQuery(id+"F0.wireOp",EDGE,"E2"),sQuery(id+"F0.wireOp",EDGE,"E10"),subQ0,sQuery(id+"F2.wireOp",EDGE,"E22")])],"isStart":false})],"blendedInto":[makeQuery(id+"F3.opExtrude","CAP_FACE",FACE,{"disambiguationData":[OSD([sQuery(id+"F0.wireOp",EDGE,"E2"),sQuery(id+"F0.wireOp",EDGE,"E10"),subQ0,sQuery(id+"F2.wireOp",EDGE,"E22")])],"isStart":false})]});}
            var Q39;
            {var subQ0=sQuery(id+"F0.wireOp",EDGE,"E16.MirrorCS");Q39=makeQuery(id+"F4.opChamfer","BLEND_EDGE",EDGE,{"blendedFrom":[makeQuery(id+"F3.opExtrude","CAP_EDGE",EDGE,{"disambiguationData":[OSD([subQ0])],"isStart":false}),makeQuery(id+"F3.opExtrude","CAP_FACE",FACE,{"disambiguationData":[OSD([sQuery(id+"F0.wireOp",EDGE,"E5.MirrorC"),sQuery(id+"F0.wireOp",EDGE,"E15.MirrorCS"),subQ0,sQuery(id+"F2.wireOp",EDGE,"E25")])],"isStart":false})],"blendedInto":[makeQuery(id+"F3.opExtrude","CAP_FACE",FACE,{"disambiguationData":[OSD([sQuery(id+"F0.wireOp",EDGE,"E5.MirrorC"),sQuery(id+"F0.wireOp",EDGE,"E15.MirrorCS"),subQ0,sQuery(id+"F2.wireOp",EDGE,"E25")])],"isStart":false})]});}
            var Q40;
            {var subQ0=sQuery(id+"F0.wireOp",EDGE,"E15.MirrorCS");Q40=makeQuery(id+"F4.opChamfer","BLEND_EDGE",EDGE,{"blendedFrom":[makeQuery(id+"F3.opExtrude","CAP_EDGE",EDGE,{"disambiguationData":[OSD([subQ0])],"isStart":false}),makeQuery(id+"F3.opExtrude","CAP_FACE",FACE,{"disambiguationData":[OSD([sQuery(id+"F0.wireOp",EDGE,"E5.MirrorC"),subQ0,sQuery(id+"F0.wireOp",EDGE,"E16.MirrorCS"),sQuery(id+"F2.wireOp",EDGE,"E25")])],"isStart":false})],"blendedInto":[makeQuery(id+"F3.opExtrude","CAP_FACE",FACE,{"disambiguationData":[OSD([sQuery(id+"F0.wireOp",EDGE,"E5.MirrorC"),subQ0,sQuery(id+"F0.wireOp",EDGE,"E16.MirrorCS"),sQuery(id+"F2.wireOp",EDGE,"E25")])],"isStart":false})]});}
            var Q41;
            {var subQ0=sQuery(id+"F0.wireOp",EDGE,"E14.MirrorCS");Q41=makeQuery(id+"F4.opChamfer","BLEND_EDGE",EDGE,{"blendedFrom":[makeQuery(id+"F3.opExtrude","CAP_EDGE",EDGE,{"disambiguationData":[OSD([subQ0])],"isStart":false}),makeQuery(id+"F3.opExtrude","CAP_FACE",FACE,{"disambiguationData":[OSD([sQuery(id+"F0.wireOp",EDGE,"E3.MirrorC"),sQuery(id+"F0.wireOp",EDGE,"E13.MirrorCS"),subQ0,sQuery(id+"F2.wireOp",EDGE,"E24")])],"isStart":false})],"blendedInto":[makeQuery(id+"F3.opExtrude","CAP_FACE",FACE,{"disambiguationData":[OSD([sQuery(id+"F0.wireOp",EDGE,"E3.MirrorC"),sQuery(id+"F0.wireOp",EDGE,"E13.MirrorCS"),subQ0,sQuery(id+"F2.wireOp",EDGE,"E24")])],"isStart":false})]});}
            var Q42;
            {var subQ0=sQuery(id+"F0.wireOp",EDGE,"E13.MirrorCS");Q42=makeQuery(id+"F4.opChamfer","BLEND_EDGE",EDGE,{"blendedFrom":[makeQuery(id+"F3.opExtrude","CAP_EDGE",EDGE,{"disambiguationData":[OSD([subQ0])],"isStart":false}),makeQuery(id+"F3.opExtrude","CAP_FACE",FACE,{"disambiguationData":[OSD([sQuery(id+"F0.wireOp",EDGE,"E3.MirrorC"),subQ0,sQuery(id+"F0.wireOp",EDGE,"E14.MirrorCS"),sQuery(id+"F2.wireOp",EDGE,"E24")])],"isStart":false})],"blendedInto":[makeQuery(id+"F3.opExtrude","CAP_FACE",FACE,{"disambiguationData":[OSD([sQuery(id+"F0.wireOp",EDGE,"E3.MirrorC"),subQ0,sQuery(id+"F0.wireOp",EDGE,"E14.MirrorCS"),sQuery(id+"F2.wireOp",EDGE,"E24")])],"isStart":false})]});}
            var Q43;
            Q43=makeQuery(id+"F1.opExtrude","CAP_EDGE",EDGE,{"disambiguationData":[OSD([sQuery(id+"F0.wireOp",EDGE,"E1")])],"isStart":false});
            var Q44;
            {var subQ0=sQuery(id+"F0.wireOp",EDGE,"E12.MirrorCS");Q44=makeQuery(id+"F4.opChamfer","BLEND_EDGE",EDGE,{"blendedFrom":[makeQuery(id+"F3.opExtrude","CAP_EDGE",EDGE,{"disambiguationData":[OSD([subQ0])],"isStart":false}),makeQuery(id+"F3.opExtrude","CAP_FACE",FACE,{"disambiguationData":[OSD([sQuery(id+"F0.wireOp",EDGE,"E4"),sQuery(id+"F0.wireOp",EDGE,"E11"),subQ0,sQuery(id+"F2.wireOp",EDGE,"E23")])],"isStart":false})],"blendedInto":[makeQuery(id+"F3.opExtrude","CAP_FACE",FACE,{"disambiguationData":[OSD([sQuery(id+"F0.wireOp",EDGE,"E4"),sQuery(id+"F0.wireOp",EDGE,"E11"),subQ0,sQuery(id+"F2.wireOp",EDGE,"E23")])],"isStart":false})]});}
            var Q45;
            {var subQ0=sQuery(id+"F0.wireOp",EDGE,"E11");Q45=makeQuery(id+"F4.opChamfer","BLEND_EDGE",EDGE,{"blendedFrom":[makeQuery(id+"F3.opExtrude","CAP_EDGE",EDGE,{"disambiguationData":[OSD([subQ0])],"isStart":false}),makeQuery(id+"F3.opExtrude","CAP_FACE",FACE,{"disambiguationData":[OSD([sQuery(id+"F0.wireOp",EDGE,"E4"),subQ0,sQuery(id+"F0.wireOp",EDGE,"E12.MirrorCS"),sQuery(id+"F2.wireOp",EDGE,"E23")])],"isStart":false})],"blendedInto":[makeQuery(id+"F3.opExtrude","CAP_FACE",FACE,{"disambiguationData":[OSD([sQuery(id+"F0.wireOp",EDGE,"E4"),subQ0,sQuery(id+"F0.wireOp",EDGE,"E12.MirrorCS"),sQuery(id+"F2.wireOp",EDGE,"E23")])],"isStart":false})]});}
            var Q46;
            Q46=makeQuery(id+"F3.opExtrude","CAP_EDGE",EDGE,{"disambiguationData":[OSD([sQuery(id+"F2.wireOp",EDGE,"E22")])],"isStart":false});
            var Q47;
            Q47=makeQuery(id+"F3.opExtrude","CAP_EDGE",EDGE,{"disambiguationData":[OSD([sQuery(id+"F2.wireOp",EDGE,"E23")])],"isStart":false});
            var Q48;
            Q48=makeQuery(id+"F3.opExtrude","CAP_EDGE",EDGE,{"disambiguationData":[OSD([sQuery(id+"F2.wireOp",EDGE,"E24")])],"isStart":false});
            var Q49;
            Q49=makeQuery(id+"F3.opExtrude","CAP_EDGE",EDGE,{"disambiguationData":[OSD([sQuery(id+"F2.wireOp",EDGE,"E25")])],"isStart":false});
            var Q50;
            Q50=makeQuery(id+"F3.opExtrude","CAP_EDGE",EDGE,{"disambiguationData":[OSD([sQuery(id+"F0.wireOp",EDGE,"E3.MirrorC")])],"isStart":true});
            var Q51;
            Q51=makeQuery(id+"F3.opExtrude","CAP_EDGE",EDGE,{"disambiguationData":[OSD([sQuery(id+"F0.wireOp",EDGE,"E4")])],"isStart":true});
            var Q52;
            Q52=makeQuery(id+"F3.opExtrude","CAP_EDGE",EDGE,{"disambiguationData":[OSD([sQuery(id+"F0.wireOp",EDGE,"E2")])],"isStart":true});
            var Q53;
            Q53=makeQuery(id+"F3.opExtrude","CAP_EDGE",EDGE,{"disambiguationData":[OSD([sQuery(id+"F0.wireOp",EDGE,"E3.MirrorC")])],"isStart":false});
            var Q54;
            Q54=makeQuery(id+"F3.opExtrude","CAP_EDGE",EDGE,{"disambiguationData":[OSD([sQuery(id+"F0.wireOp",EDGE,"E4")])],"isStart":false});
            var Q55;
            Q55=makeQuery(id+"F3.opExtrude","CAP_EDGE",EDGE,{"disambiguationData":[OSD([sQuery(id+"F0.wireOp",EDGE,"E5.MirrorC")])],"isStart":false});
            var Q56;
            Q56=makeQuery(id+"F3.opExtrude","CAP_EDGE",EDGE,{"disambiguationData":[OSD([sQuery(id+"F0.wireOp",EDGE,"E2")])],"isStart":false});
            fillet(context, id + "F6", {"entities" : qUnion([Q0, Q1, Q2, Q3, Q4, Q5, Q6, Q7, Q8, Q9, Q10, Q11, Q12, Q13, Q14, Q15, Q16, Q17, Q18, Q19, Q20, Q21, Q22, Q23, Q24, Q25, Q26, Q27, Q28, Q29, Q30, Q31, Q32, Q33, Q34, Q35, Q36, Q37, Q38, Q39, Q40, Q41, Q42, Q43, Q44, Q45, Q46, Q47, Q48, Q49, Q50, Q51, Q52, Q53, Q54, Q55, Q56]), "radius" : 1 * mm, "tangentPropagation" : true, "allowEdgeOverflow" : false});
        }
    });
